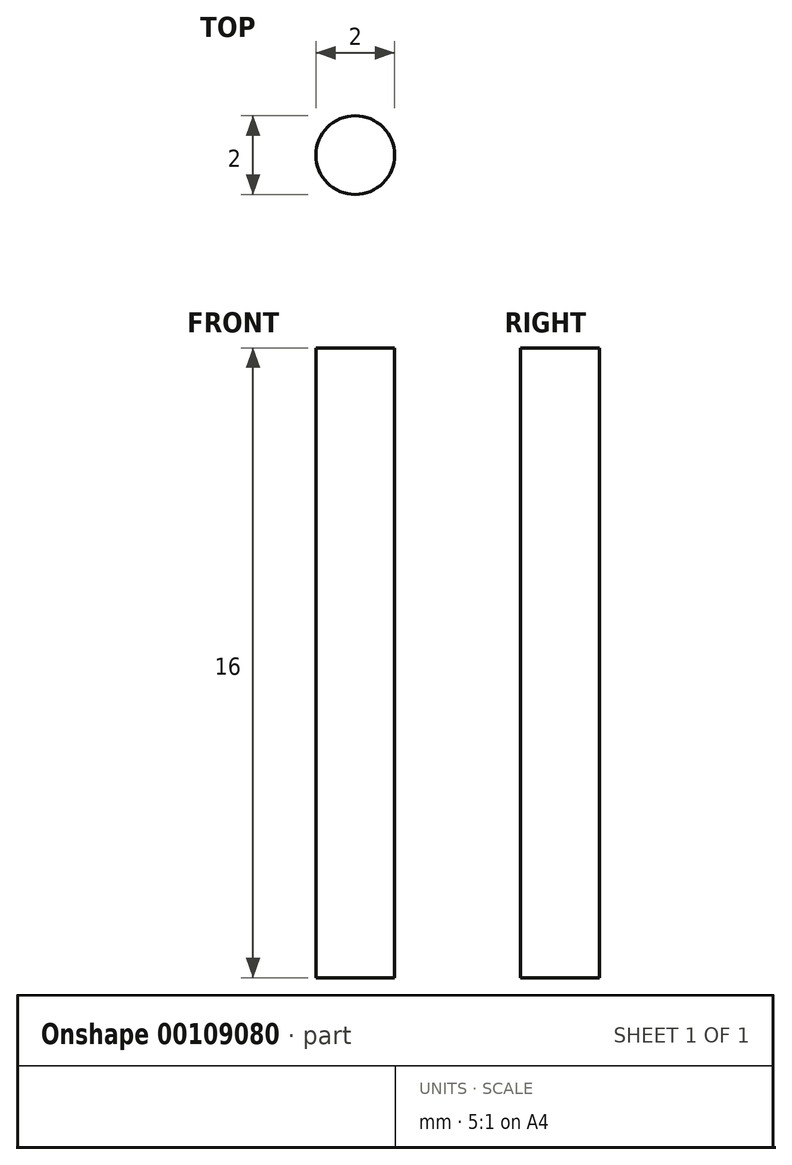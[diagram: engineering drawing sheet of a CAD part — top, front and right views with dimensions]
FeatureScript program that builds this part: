
annotation { "Feature Type Name" : "Feature", "Feature Type Description" : "" }
export const myFeature = defineFeature(function(context is Context, id is Id, definition is map)
    precondition{}
    {
        {
            var Q0;
            Q0=qCreatedBy(makeId("Top.planeOp"),FACE);
            var sketch = newSketch(context, id + "F0", { "sketchPlane" : qUnion([Q0])});
            skCircle(sketch, "E0", {"center": v(0, 0) * mm, "radius": 1 * mm});
            skSolve(sketch);
        }
        {
            var Q0;
            Q0=makeQuery(id+"F0.imprint","IMPRINT",FACE,{"disambiguationData":[TD([[makeQuery(id+"F0.imprint","IMPRINT",EDGE,{"derivedFrom":sQuery(id+"F0.wireOp",EDGE,"E0")}),1.0]])]});
            extrude(context, id + "F1", {"entities" : qUnion([Q0]), "endBound" : BoundingType.SYMMETRIC, "depth" : 16 * mm});
        }
    });
